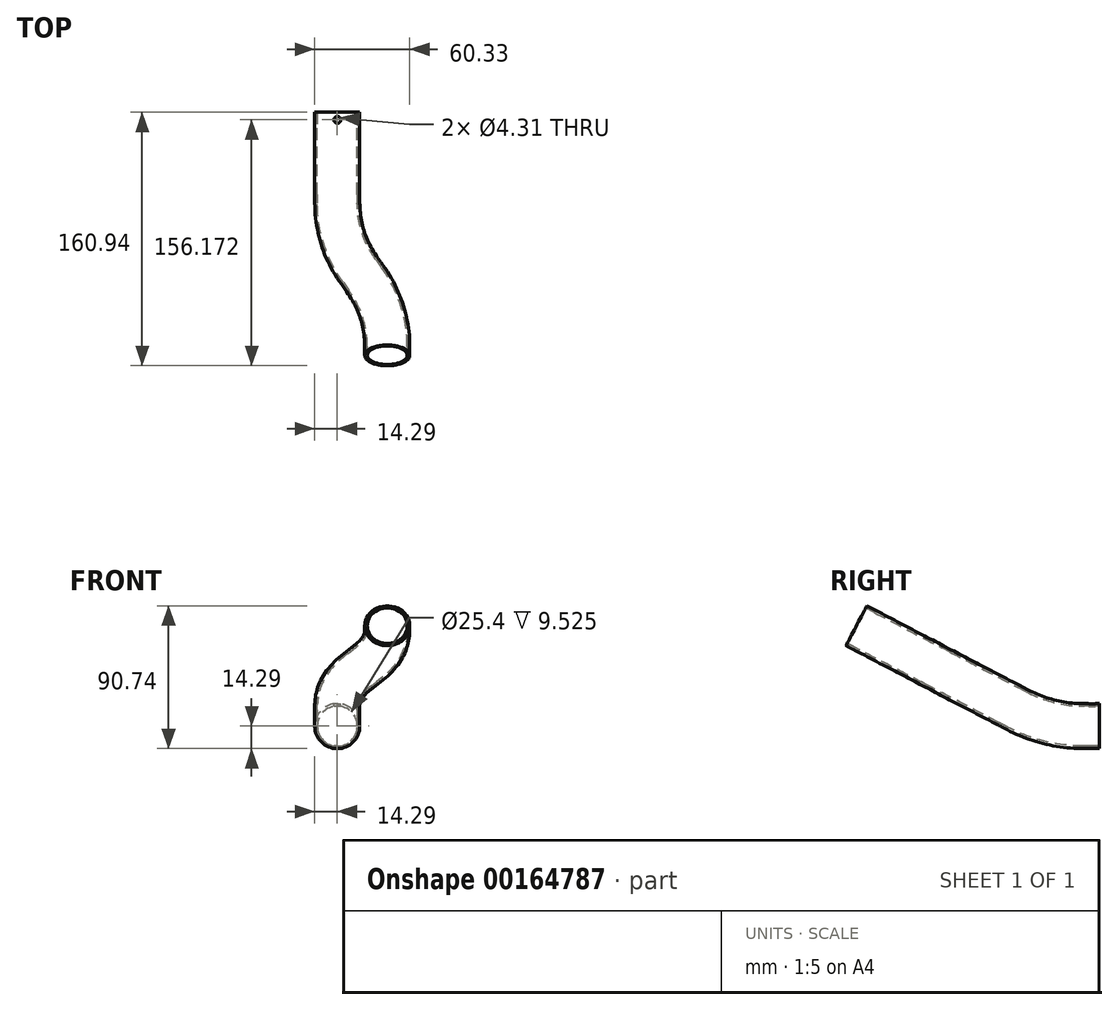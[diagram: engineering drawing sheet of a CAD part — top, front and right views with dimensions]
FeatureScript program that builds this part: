
annotation { "Feature Type Name" : "Feature", "Feature Type Description" : "" }
export const myFeature = defineFeature(function(context is Context, id is Id, definition is map)
    precondition{}
    {
        {
            var Q0;
            Q0=qCreatedBy(makeId("Front.planeOp"),FACE);
            var sketch = newSketch(context, id + "F0", { "sketchPlane" : qUnion([Q0])});
            skCircle(sketch, "E0", {"center": v(0, 0) * mm, "radius": 12.7 * mm});
            skCircle(sketch, "E1", {"center": v(0, 0) * mm, "radius": 14.29 * mm, "construction": true});
            skLineSegment(sketch, "E2.bottom", {"start": v(-14.29, -14.29) * mm, "end": v(14.29, -14.29) * mm});
            skLineSegment(sketch, "E2.top", {"start": v(-14.29, 14.29) * mm, "end": v(14.29, 14.29) * mm});
            skLineSegment(sketch, "E2.left", {"start": v(-14.29, -14.29) * mm, "end": v(-14.29, 14.29) * mm});
            skLineSegment(sketch, "E2.right", {"start": v(14.29, -14.29) * mm, "end": v(14.29, 14.29) * mm});
            skSolve(sketch);
        }
        {
            var Q0;
            Q0=qCreatedBy(makeId("Right.planeOp"),FACE);
            var sketch = newSketch(context, id + "F1", { "sketchPlane" : qUnion([Q0])});
            skArc(sketch, "E3", {"start": v(-42.6, 10.45) * mm, "mid": v(-21.93, 2.65) * mm, "end": v(0, 0) * mm});
            skLineSegment(sketch, "E4", {"start": v(0, 0) * mm, "end": v(25.4, 0) * mm, "construction": true});
            skLineSegment(sketch, "E5", {"start": v(-42.6, 10.45) * mm, "end": v(25.4, -25.04) * mm, "construction": true});
            skLineSegment(sketch, "E6", {"start": v(25.4, 0) * mm, "end": v(25.4, -25.04) * mm, "construction": true});
            skLineSegment(sketch, "E7", {"start": v(-42.6, 10.45) * mm, "end": v(-48.23, 13.38) * mm});
            skLineSegment(sketch, "E8", {"start": v(25.4, -25.04) * mm, "end": v(85.73, -56.51) * mm, "construction": true});
            skCircle(sketch, "E9", {"center": v(85.72, -56.52) * mm, "radius": 72.4 * mm});
            skLineSegment(sketch, "E10", {"start": v(25.4, 0) * mm, "end": v(25.4, 15.88) * mm, "construction": true});
            skLineSegment(sketch, "E11", {"start": v(25.4, 15.88) * mm, "end": v(85.72, 15.88) * mm, "construction": true});
            skLineSegment(sketch, "E12", {"start": v(25.4, 15.88) * mm, "end": v(0, 15.88) * mm, "construction": true});
            skArc(sketch, "E13", {"start": v(-35.25, 24.52) * mm, "mid": v(-18.15, 18.07) * mm, "end": v(0, 15.87) * mm, "construction": true});
            skLineSegment(sketch, "E14", {"start": v(-42.6, 10.45) * mm, "end": v(-35.25, 24.52) * mm, "construction": true});
            skLineSegment(sketch, "E15.bottom", {"start": v(134.1, -8.13) * mm, "end": v(37.34, -8.13) * mm, "construction": true});
            skLineSegment(sketch, "E15.top", {"start": v(134.1, -104.9) * mm, "end": v(37.34, -104.9) * mm, "construction": true});
            skLineSegment(sketch, "E15.left", {"start": v(134.1, -8.13) * mm, "end": v(134.1, -104.9) * mm, "construction": true});
            skLineSegment(sketch, "E15.right", {"start": v(37.34, -8.13) * mm, "end": v(37.34, -104.9) * mm, "construction": true});
            skPoint(sketch, "E15.middle", {"position": v(85.73, -56.51) * mm});
            skCircle(sketch, "E16", {"center": v(134.1, -8.13) * mm, "radius": 3.97 * mm, "construction": true});
            skLineSegment(sketch, "E17", {"start": v(85.73, -56.51) * mm, "end": v(37.34, -56.52) * mm, "construction": true});
            skSolve(sketch);
        }
        {
            var Q0;
            Q0=makeQuery(id+"F0.imprint","IMPRINT",FACE,{"disambiguationData":[TD([[makeQuery(id+"F0.imprint","IMPRINT",EDGE,{"derivedFrom":sQuery(id+"F0.wireOp",EDGE,"E0")}),-1.0]])]});
            var Q1;
            Q1=sQuery(id+"F1.wireOp",EDGE,"E3");
            var Q2;
            Q2=sQuery(id+"F1.wireOp",EDGE,"E7");
            sweep(context, id + "F2", {"profiles" : qUnion([Q0]), "path" : qUnion([Q1, Q2])});
        }
        {
            var Q0;
            Q0=makeQuery(id+"F2.opSweep","CAP_FACE",FACE,{"disambiguationData":[OSD([sQuery(id+"F0.wireOp",EDGE,"E0"),sQuery(id+"F0.wireOp",EDGE,"E1"),sQuery(id+"F1.wireOp",VERTEX,"E3.end")])],"isStart":true});
            extrude(context, id + "F3", {"entities" : qUnion([Q0]), "operationType" : NewBodyOperationType.ADD, "depth" : 9.52 * mm});
        }
        {
            var Q0;
            Q0=qCreatedBy(makeId("Top.planeOp"),FACE);
            var sketch = newSketch(context, id + "F4", { "sketchPlane" : qUnion([Q0])});
            skLineSegment(sketch, "E18", {"start": v(0, 0) * mm, "end": v(0, 9.53) * mm, "construction": true});
            skCircle(sketch, "E19", {"center": v(0, 4.76) * mm, "radius": 2.15 * mm});
            skSolve(sketch);
        }
        {
            var Q0;
            Q0 = qSketchRegion(id + "F4", true);
            var Q1;
            Q1=makeQuery(id+"F3.opExtrude","SWEPT_FACE",FACE,{"disambiguationData":[OSD([sQuery(id+"F0.wireOp",EDGE,"E1"),sQuery(id+"F1.wireOp",VERTEX,"E3.end")])]});
            var Q2;
            Q2=makeQuery(id+"F3.opExtrude","SWEPT_FACE",FACE,{"disambiguationData":[OSD([sQuery(id+"F0.wireOp",EDGE,"E1"),sQuery(id+"F1.wireOp",VERTEX,"E3.end")])]});
            extrude(context, id + "F5", {"entities" : qUnion([Q0]), "operationType" : NewBodyOperationType.REMOVE, "endBound" : BoundingType.THROUGH_ALL, "oppositeDirection" : true, "endBoundEntityFace" : qUnion([Q1]), "depth" : 25.4 * mm, "hasSecondDirection" : true, "secondDirectionBound" : SecondDirectionBoundingType.THROUGH_ALL, "secondDirectionOppositeDirection" : false, "secondDirectionBoundEntityFace" : qUnion([Q2]), "secondDirectionDepth" : 25.4 * mm});
        }
        {
            var Q0;
            Q0=makeQuery(id+"F2.opSweep","SWEPT_FACE",FACE,{"disambiguationData":[OSD([sQuery(id+"F0.wireOp",EDGE,"E2.bottom"),sQuery(id+"F1.wireOp",EDGE,"E7")])]});
            var sketch = newSketch(context, id + "F6", { "sketchPlane" : qUnion([Q0])});
            skArc(sketch, "E20", {"start": v(26.22, 89.89) * mm, "mid": v(17.33, 70.27) * mm, "end": v(14.29, 48.95) * mm});
            skLineSegment(sketch, "E21", {"start": v(26.22, 89.89) * mm, "end": v(29.63, 95.24) * mm});
            skArc(sketch, "E22", {"start": v(29.63, 95.24) * mm, "mid": v(41.85, 122.22) * mm, "end": v(46.04, 151.53) * mm});
            skArc(sketch, "E23", {"start": v(2.12, 105.24) * mm, "mid": v(-10.1, 78.26) * mm, "end": v(-14.29, 48.95) * mm, "construction": true});
            skLineSegment(sketch, "E24", {"start": v(2.12, 105.24) * mm, "end": v(5.53, 110.6) * mm, "construction": true});
            skLineSegment(sketch, "E25", {"start": v(26.22, 89.89) * mm, "end": v(2.12, 105.24) * mm, "construction": true});
            skLineSegment(sketch, "E26", {"start": v(5.53, 110.6) * mm, "end": v(29.63, 95.24) * mm, "construction": true});
            skArc(sketch, "E27", {"start": v(5.53, 110.6) * mm, "mid": v(14.42, 130.21) * mm, "end": v(17.46, 151.53) * mm, "construction": true});
            skLineSegment(sketch, "E28", {"start": v(17.46, 151.53) * mm, "end": v(46.04, 151.53) * mm, "construction": true});
            skLineSegment(sketch, "E29", {"start": v(-58.74, 151.53) * mm, "end": v(17.46, 151.53) * mm, "construction": true});
            skLineSegment(sketch, "E30", {"start": v(14.29, 48.95) * mm, "end": v(46.04, 48.95) * mm, "construction": true});
            skLineSegment(sketch, "E31", {"start": v(46.04, 48.95) * mm, "end": v(46.04, 151.53) * mm, "construction": true});
            skLineSegment(sketch, "E32", {"start": v(46.04, 151.53) * mm, "end": v(46.04, 157.88) * mm});
            skSolve(sketch);
        }
        {
            var Q0;
            Q0=makeQuery(id+"F2.opSweep","CAP_FACE",FACE,{"disambiguationData":[OSD([sQuery(id+"F0.wireOp",EDGE,"E0"),sQuery(id+"F0.wireOp",EDGE,"E2.bottom"),sQuery(id+"F0.wireOp",EDGE,"E2.top"),sQuery(id+"F0.wireOp",EDGE,"E2.left"),sQuery(id+"F0.wireOp",EDGE,"E2.right"),sQuery(id+"F1.wireOp",VERTEX,"E7.end")])],"isStart":false});
            var Q1;
            Q1=sQuery(id+"F6.wireOp",EDGE,"E20");
            var Q2;
            Q2=sQuery(id+"F6.wireOp",EDGE,"E21");
            var Q3;
            Q3=sQuery(id+"F6.wireOp",EDGE,"E22");
            var Q4;
            Q4=sQuery(id+"F6.wireOp",EDGE,"E32");
            sweep(context, id + "F7", {"operationType" : NewBodyOperationType.ADD, "profiles" : qUnion([Q0]), "path" : qUnion([Q1, Q2, Q3, Q4])});
        }
        {
            var Q0;
            Q0=makeQuery(id+"F3.opExtrude","SWEPT_EDGE",EDGE,{"disambiguationData":[OSD([sQuery(id+"F0.wireOp",EDGE,"E2.bottom"),sQuery(id+"F0.wireOp",EDGE,"E2.left"),sQuery(id+"F1.wireOp",EDGE,"E3")])]});
            var Q1;
            Q1=makeQuery(id+"F3.opExtrude","SWEPT_EDGE",EDGE,{"disambiguationData":[OSD([sQuery(id+"F0.wireOp",EDGE,"E2.bottom"),sQuery(id+"F0.wireOp",EDGE,"E2.right"),sQuery(id+"F1.wireOp",EDGE,"E3")])]});
            var Q2;
            Q2=makeQuery(id+"F3.opExtrude","SWEPT_EDGE",EDGE,{"disambiguationData":[OSD([sQuery(id+"F0.wireOp",EDGE,"E2.top"),sQuery(id+"F0.wireOp",EDGE,"E2.left"),sQuery(id+"F1.wireOp",EDGE,"E3")])]});
            var Q3;
            Q3=makeQuery(id+"F3.opExtrude","SWEPT_EDGE",EDGE,{"disambiguationData":[OSD([sQuery(id+"F0.wireOp",EDGE,"E2.top"),sQuery(id+"F0.wireOp",EDGE,"E2.right"),sQuery(id+"F1.wireOp",EDGE,"E3")])]});
            fillet(context, id + "F8", {"entities" : qUnion([Q0, Q1, Q2, Q3]), "radius" : 14.29 * mm, "tangentPropagation" : true, "allowEdgeOverflow" : false});
        }
    });
